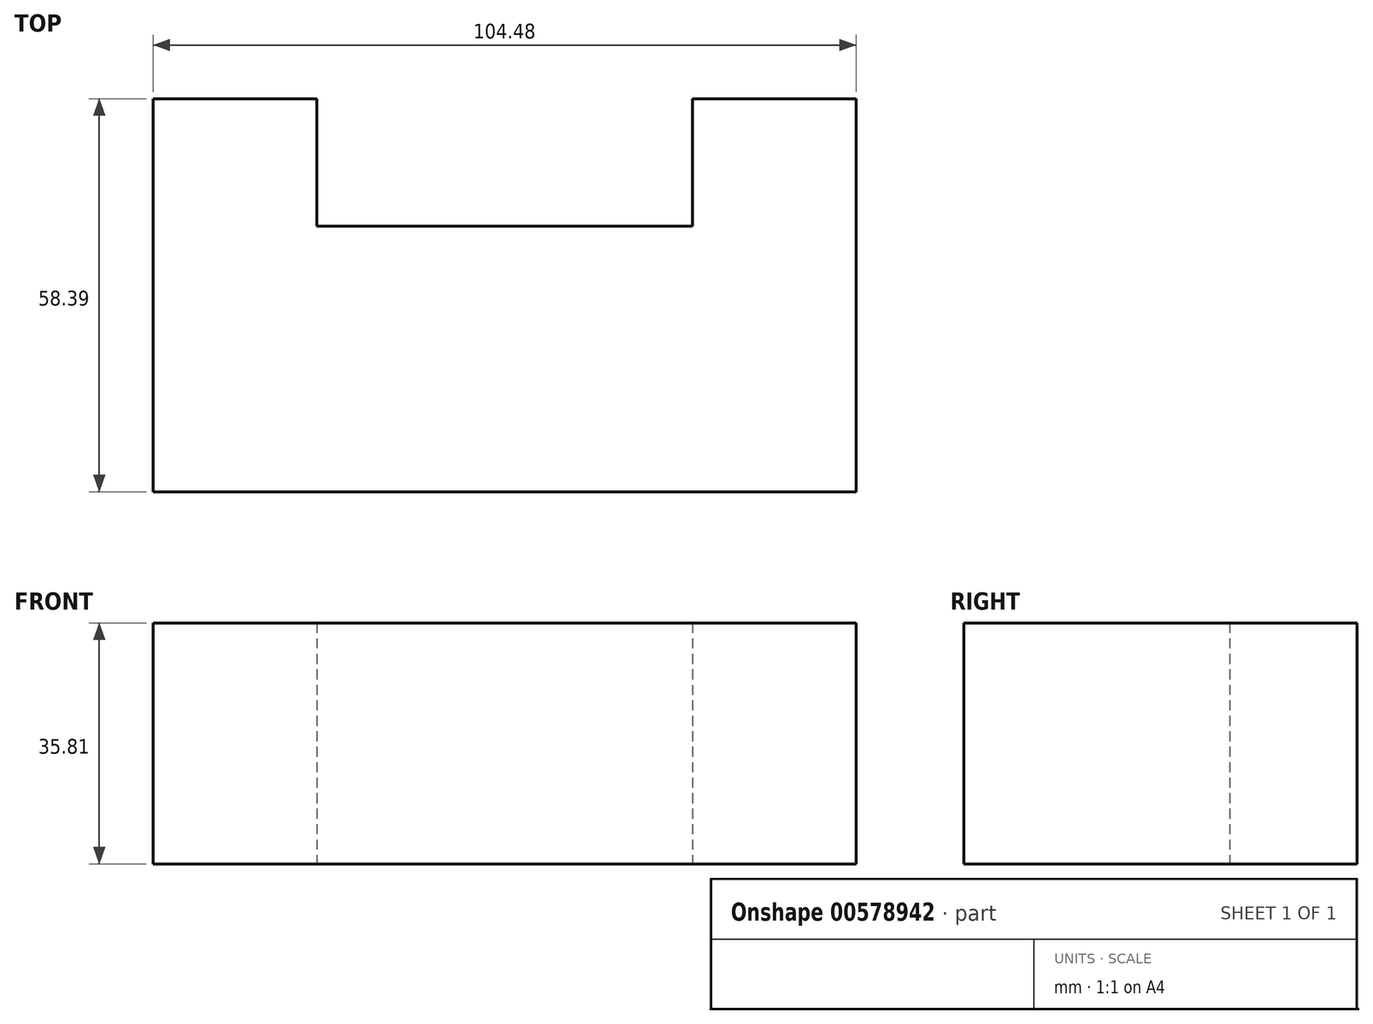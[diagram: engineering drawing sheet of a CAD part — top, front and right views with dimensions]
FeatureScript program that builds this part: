
annotation { "Feature Type Name" : "Feature", "Feature Type Description" : "" }
export const myFeature = defineFeature(function(context is Context, id is Id, definition is map)
    precondition{}
    {
        {
            var Q0;
            Q0=qCreatedBy(makeId("Top.planeOp"),FACE);
            var sketch = newSketch(context, id + "F0", { "sketchPlane" : qUnion([Q0])});
            skLineSegment(sketch, "E0", {"start": v(-52.24, 0) * mm, "end": v(-52.24, 58.4) * mm});
            skLineSegment(sketch, "E1", {"start": v(-52.24, 58.4) * mm, "end": v(-27.92, 58.4) * mm});
            skLineSegment(sketch, "E2", {"start": v(-27.92, 58.4) * mm, "end": v(-27.92, 39.48) * mm});
            skLineSegment(sketch, "E3", {"start": v(-27.92, 39.48) * mm, "end": v(27.92, 39.48) * mm});
            skLineSegment(sketch, "E4", {"start": v(27.92, 39.48) * mm, "end": v(27.92, 58.4) * mm});
            skLineSegment(sketch, "E5", {"start": v(27.92, 58.4) * mm, "end": v(52.24, 58.4) * mm});
            skLineSegment(sketch, "E6", {"start": v(52.24, 58.4) * mm, "end": v(52.24, 0) * mm});
            skLineSegment(sketch, "E7", {"start": v(52.24, 0) * mm, "end": v(-52.24, 0) * mm});
            skSolve(sketch);
        }
        {
            var Q0;
            Q0 = qSketchRegion(id + "F0", true);
            extrude(context, id + "F1", {"entities" : qUnion([Q0]), "depth" : 35.81 * mm, "offsetDistance" : 25.4 * mm});
        }
    });
